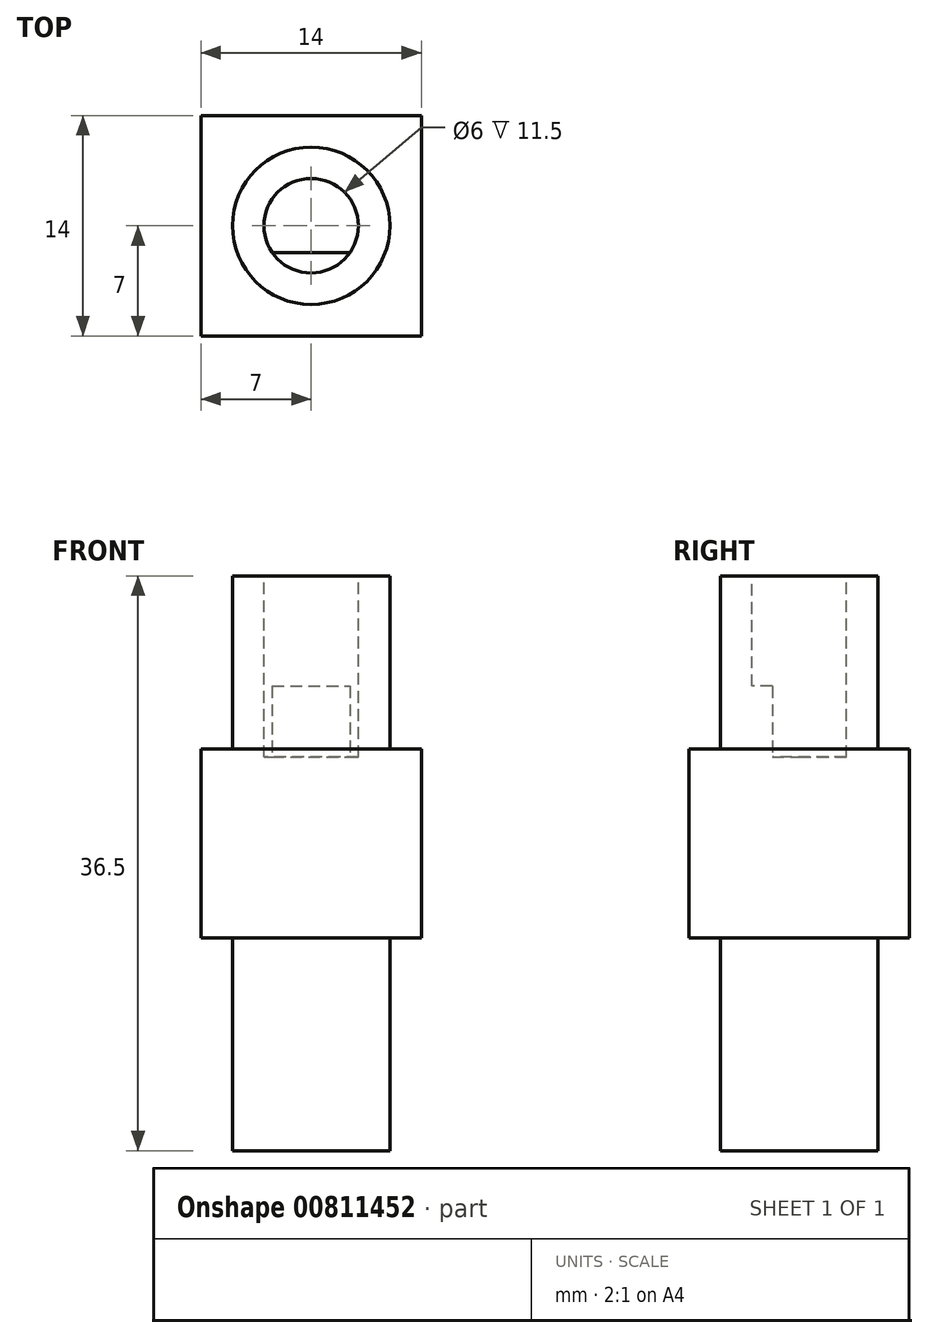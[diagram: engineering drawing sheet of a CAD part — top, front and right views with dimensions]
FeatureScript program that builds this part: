
annotation { "Feature Type Name" : "Feature", "Feature Type Description" : "" }
export const myFeature = defineFeature(function(context is Context, id is Id, definition is map)
    precondition{}
    {
        {
            var Q0;
            Q0=qCreatedBy(makeId("Top.planeOp"),FACE);
            var sketch = newSketch(context, id + "F0", { "sketchPlane" : qUnion([Q0])});
            skCircle(sketch, "E0", {"center": v(0, 0) * mm, "radius": 5 * mm});
            skSolve(sketch);
        }
        {
            var Q0;
            Q0 = qSketchRegion(id + "F0", true);
            extrude(context, id + "F1", {"entities" : qUnion([Q0]), "depth" : 13.5 * mm, "offsetDistance" : 25 * mm});
        }
        {
            var Q0;
            Q0=makeQuery(id+"F1.opExtrude","CAP_FACE",FACE,{"disambiguationData":[OSD([sQuery(id+"F0.wireOp",EDGE,"E0")])],"isStart":false});
            var sketch = newSketch(context, id + "F2", { "sketchPlane" : qUnion([Q0])});
            skLineSegment(sketch, "E1.bottom", {"start": v(-7, 7) * mm, "end": v(7, 7) * mm});
            skLineSegment(sketch, "E1.top", {"start": v(-7, -7) * mm, "end": v(7, -7) * mm});
            skLineSegment(sketch, "E1.left", {"start": v(-7, 7) * mm, "end": v(-7, -7) * mm});
            skLineSegment(sketch, "E1.right", {"start": v(7, 7) * mm, "end": v(7, -7) * mm});
            skSolve(sketch);
        }
        {
            var Q0;
            Q0 = qSketchRegion(id + "F2", true);
            extrude(context, id + "F3", {"entities" : qUnion([Q0]), "operationType" : NewBodyOperationType.ADD, "depth" : 12 * mm, "offsetDistance" : 25 * mm});
        }
        {
            var Q0;
            Q0=makeQuery(id+"F3.opExtrude","CAP_FACE",FACE,{"disambiguationData":[OSD([sQuery(id+"F2.wireOp",EDGE,"E1.bottom"),sQuery(id+"F2.wireOp",EDGE,"E1.top"),sQuery(id+"F2.wireOp",EDGE,"E1.left"),sQuery(id+"F2.wireOp",EDGE,"E1.right")])],"isStart":false});
            var sketch = newSketch(context, id + "F4", { "sketchPlane" : qUnion([Q0])});
            skCircle(sketch, "E2", {"center": v(0, 0) * mm, "radius": 5 * mm});
            skSolve(sketch);
        }
        {
            var Q0;
            Q0 = qSketchRegion(id + "F4", true);
            extrude(context, id + "F5", {"entities" : qUnion([Q0]), "operationType" : NewBodyOperationType.ADD, "depth" : 11 * mm, "offsetDistance" : 25 * mm});
        }
        {
            var Q0;
            Q0=makeQuery(id+"F5.opExtrude","CAP_FACE",FACE,{"disambiguationData":[OSD([sQuery(id+"F4.wireOp",EDGE,"E2")])],"isStart":false});
            var sketch = newSketch(context, id + "F6", { "sketchPlane" : qUnion([Q0])});
            skCircle(sketch, "E3", {"center": v(0, 0) * mm, "radius": 3 * mm});
            skSolve(sketch);
        }
        {
            var Q0;
            Q0 = qSketchRegion(id + "F6", true);
            extrude(context, id + "F7", {"entities" : qUnion([Q0]), "operationType" : NewBodyOperationType.REMOVE, "oppositeDirection" : true, "depth" : 11.5 * mm, "offsetDistance" : 25 * mm});
        }
        {
            var Q0;
            Q0=makeQuery(id+"F7.boolean.opBoolean","COPY",FACE,{"derivedFrom":makeQuery(id+"F7.opExtrude","CAP_FACE",FACE,{"disambiguationData":[OSD([sQuery(id+"F6.wireOp",EDGE,"E3")])],"isStart":false})});
            var sketch = newSketch(context, id + "F8", { "sketchPlane" : qUnion([Q0])});
            skLineSegment(sketch, "E4", {"start": v(-2.47, -1.7) * mm, "end": v(2.47, -1.7) * mm});
            skSolve(sketch);
        }
        {
            var Q0;
            {var subQ0=sQuery(id+"F8.wireOp",EDGE,"E4");Q0=makeQuery(id+"F8.imprint","IMPRINT",FACE,{"disambiguationData":[TD([[makeQuery(id+"F8.imprint","IMPRINT",EDGE,{"derivedFrom":subQ0}),-1.0]])]});}
            extrude(context, id + "F9", {"entities" : qUnion([Q0]), "operationType" : NewBodyOperationType.ADD, "depth" : 4.5 * mm, "offsetDistance" : 25 * mm});
        }
    });
